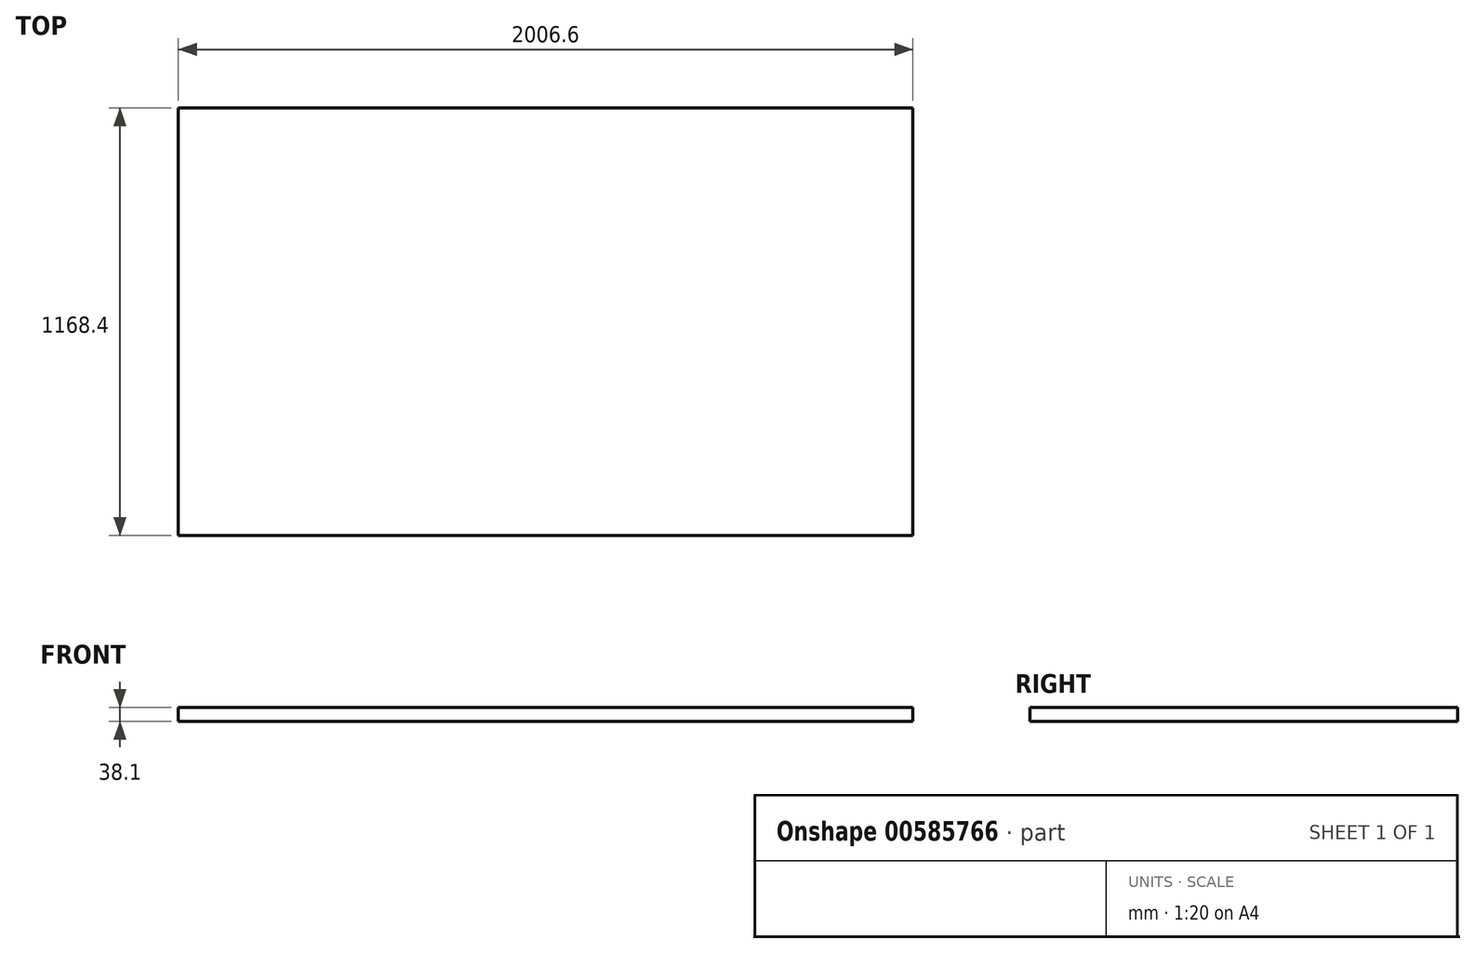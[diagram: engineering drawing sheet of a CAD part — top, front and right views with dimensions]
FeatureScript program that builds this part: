
annotation { "Feature Type Name" : "Feature", "Feature Type Description" : "" }
export const myFeature = defineFeature(function(context is Context, id is Id, definition is map)
    precondition{}
    {
        {
            var Q0;
            Q0=qCreatedBy(makeId("Top.planeOp"),FACE);
            var sketch = newSketch(context, id + "F0", { "sketchPlane" : qUnion([Q0])});
            skLineSegment(sketch, "E0", {"start": v(0, 0) * mm, "end": v(-2006.6, 0) * mm});
            skLineSegment(sketch, "E1", {"start": v(-2006.6, 0) * mm, "end": v(-2006.6, -1168.4) * mm});
            skLineSegment(sketch, "E2", {"start": v(-2006.6, -1168.4) * mm, "end": v(0, -1168.4) * mm});
            skLineSegment(sketch, "E3", {"start": v(0, -1168.4) * mm, "end": v(0, 0) * mm});
            skSolve(sketch);
        }
        {
            var Q0;
            Q0=qSketchRegion(id+"F0",true);
            extrude(context, id + "F1", {"entities" : qUnion([Q0]), "depth" : 38.1 * mm, "offsetDistance" : 25.4 * mm});
        }
    });
